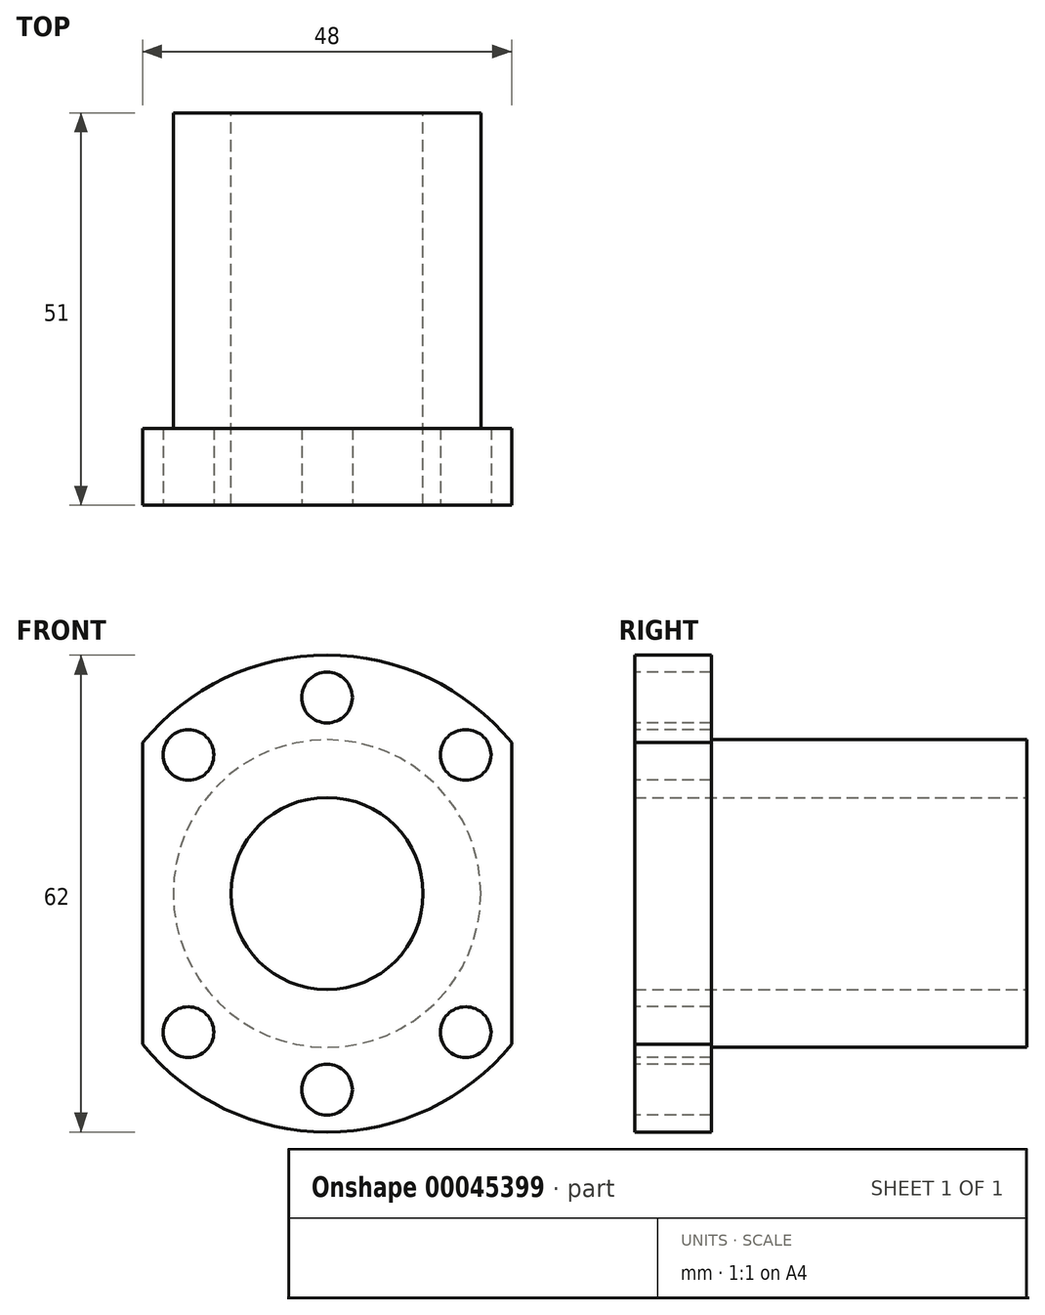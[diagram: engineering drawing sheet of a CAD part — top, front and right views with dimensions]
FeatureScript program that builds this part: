
annotation { "Feature Type Name" : "Feature", "Feature Type Description" : "" }
export const myFeature = defineFeature(function(context is Context, id is Id, definition is map)
    precondition{}
    {
        {
            var Q0;
            Q0=qCreatedBy(makeId("Front.planeOp"),FACE);
            var sketch = newSketch(context, id + "F0", { "sketchPlane" : qUnion([Q0])});
            skCircle(sketch, "E0", {"center": v(0, 0) * mm, "radius": 20 * mm});
            skCircle(sketch, "E1", {"center": v(0, 0) * mm, "radius": 12.5 * mm});
            skSolve(sketch);
        }
        {
            var Q0;
            Q0=makeQuery(id+"F0.imprint","IMPRINT",FACE,{"disambiguationData":[TD([[makeQuery(id+"F0.imprint","IMPRINT",EDGE,{"derivedFrom":sQuery(id+"F0.wireOp",EDGE,"E0")}),1.0]])]});
            extrude(context, id + "F1", {"entities" : qUnion([Q0]), "depth" : 51 * mm});
        }
        {
            var Q0;
            Q0=makeQuery(id+"F1.opExtrude","CAP_FACE",FACE,{"disambiguationData":[OSD([sQuery(id+"F0.wireOp",EDGE,"E0"),sQuery(id+"F0.wireOp",EDGE,"E1")])],"isStart":false});
            var sketch = newSketch(context, id + "F2", { "sketchPlane" : qUnion([Q0])});
            skArc(sketch, "E2", {"start": v(-24, -19.62) * mm, "mid": v(0, -31) * mm, "end": v(24, -19.62) * mm});
            skLineSegment(sketch, "E3.left", {"start": v(-24, 19.62) * mm, "end": v(-24, -19.62) * mm});
            skLineSegment(sketch, "E3.right", {"start": v(24, 19.62) * mm, "end": v(24, -19.62) * mm});
            skArc(sketch, "E4.trimOffspring", {"start": v(24, 19.62) * mm, "mid": v(0, 31) * mm, "end": v(-24, 19.62) * mm});
            skCircle(sketch, "E5", {"center": v(0, 25.5) * mm, "radius": 3.3 * mm});
            skCircle(sketch, "E6", {"center": v(0, -25.5) * mm, "radius": 3.3 * mm});
            skCircle(sketch, "E7.1.0", {"center": v(-18.03, 18.03) * mm, "radius": 3.3 * mm});
            skCircle(sketch, "E7.3.0", {"center": v(-18.03, -18.03) * mm, "radius": 3.3 * mm});
            skCircle(sketch, "E7.5.0", {"center": v(18.03, -18.03) * mm, "radius": 3.3 * mm});
            skCircle(sketch, "E7.7.0", {"center": v(18.03, 18.03) * mm, "radius": 3.3 * mm});
            skSolve(sketch);
        }
        {
            var Q0;
            Q0=makeQuery(id+"F2.imprint","IMPRINT",FACE,{"disambiguationData":[TD([[makeQuery(id+"F2.imprint","IMPRINT",EDGE,{"derivedFrom":makeQuery(id+"F1.opExtrude","CAP_EDGE",EDGE,{"disambiguationData":[OSD([sQuery(id+"F0.wireOp",EDGE,"E0")])],"isStart":false})}),1.0]])]});
            var Q1;
            Q1=makeQuery(id+"F2.imprint","IMPRINT",FACE,{"disambiguationData":[TD([[makeQuery(id+"F2.imprint","IMPRINT",EDGE,{"derivedFrom":sQuery(id+"F2.wireOp",EDGE,"E2")}),1.0]])]});
            extrude(context, id + "F3", {"entities" : qUnion([Q0, Q1]), "operationType" : NewBodyOperationType.ADD, "oppositeDirection" : true, "depth" : 10 * mm});
        }
    });
